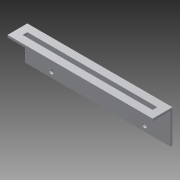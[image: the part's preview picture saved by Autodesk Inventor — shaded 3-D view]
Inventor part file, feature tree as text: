
AUTODESK INVENTOR PART (.ipt)
format: ipt  version: 2015 (Build 190159000, 159)  size: 134,656 bytes
history: native  units: mm
features: sketch x4, extrude x3, other x1, hole x1
ambient origin geometry x8: Origin, YZ Plane, XZ Plane, XY Plane, X Axis, Y Axis, Z Axis, Center Point
bodies: Body1 (feature_tree)
feature tree (9):
  other  "ソリッド1"
  extrude  "押し出し1"  Depth=11.5mm
  extrude  "押し出し2"  Depth=95.0mm
  extrude  "押し出し3"  Depth=1.5mm TaperAngle=0.0deg
  hole  "穴1"  [1 undecoded]
  sketch  "スケッチ1"
  sketch  "スケッチ2"
  sketch  "スケッチ3"
  sketch  "スケッチ4"
note: 1 required parameter value undecoded (feature->parameter linkage not recoverable at this tier; creation-order binding heuristic only, values carry confidence <= 0.55)
